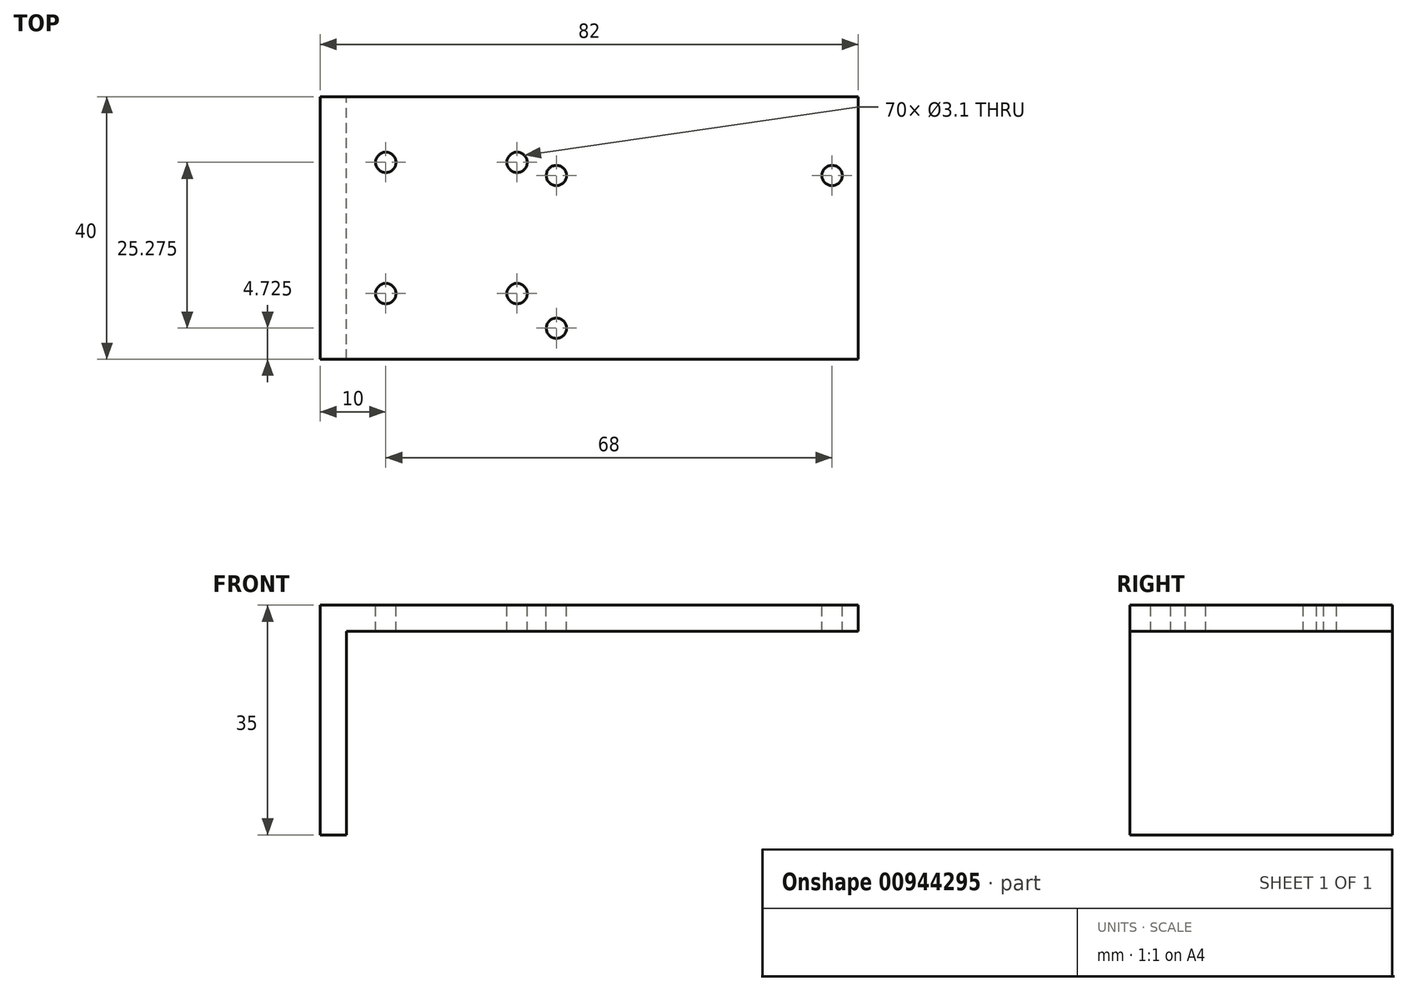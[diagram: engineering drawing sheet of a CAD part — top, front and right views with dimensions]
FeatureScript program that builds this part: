
annotation { "Feature Type Name" : "Feature", "Feature Type Description" : "" }
export const myFeature = defineFeature(function(context is Context, id is Id, definition is map)
    precondition{}
    {
        {
            var Q0;
            Q0=qCreatedBy(makeId("Front.planeOp"),FACE);
            var sketch = newSketch(context, id + "F0", { "sketchPlane" : qUnion([Q0])});
            skLineSegment(sketch, "E0", {"start": v(0, 0) * mm, "end": v(0, -35) * mm});
            skLineSegment(sketch, "E1", {"start": v(0, -35) * mm, "end": v(4, -35) * mm});
            skLineSegment(sketch, "E2", {"start": v(4, -35) * mm, "end": v(4, -4) * mm});
            skLineSegment(sketch, "E3", {"start": v(4, -4) * mm, "end": v(82, -4) * mm});
            skLineSegment(sketch, "E4", {"start": v(82, -4) * mm, "end": v(82, 0) * mm});
            skLineSegment(sketch, "E5", {"start": v(82, 0) * mm, "end": v(0, 0) * mm});
            skSolve(sketch);
        }
        {
            var Q0;
            Q0=makeQuery(id+"F0.imprint","IMPRINT",FACE,{"disambiguationData":[TD([[makeQuery(id+"F0.imprint","IMPRINT",EDGE,{"derivedFrom":sQuery(id+"F0.wireOp",EDGE,"E0")}),1.0]])]});
            extrude(context, id + "F1", {"entities" : qUnion([Q0]), "depth" : 40 * mm, "offsetDistance" : 25 * mm});
        }
        {
            var Q0;
            Q0=makeQuery(id+"F1.opExtrude","SWEPT_FACE",FACE,{"disambiguationData":[OSD([sQuery(id+"F0.wireOp",EDGE,"E5")])]});
            var sketch = newSketch(context, id + "F2", { "sketchPlane" : qUnion([Q0])});
            skLineSegment(sketch, "E6", {"start": v(0, -20) * mm, "end": v(82, -20) * mm, "construction": true});
            skLineSegment(sketch, "E7", {"start": v(20, 0) * mm, "end": v(20, -40) * mm, "construction": true});
            skCircle(sketch, "E8", {"center": v(30, -10) * mm, "radius": 1.55 * mm});
            skCircle(sketch, "E9.MirrorC", {"center": v(10, -10) * mm, "radius": 1.55 * mm});
            skCircle(sketch, "E10.MirrorC", {"center": v(10, -30) * mm, "radius": 1.55 * mm});
            skCircle(sketch, "E11.MirrorC", {"center": v(30, -30) * mm, "radius": 1.55 * mm});
            skLineSegment(sketch, "E12", {"start": v(36, -40) * mm, "end": v(36, 0) * mm, "construction": true});
            skCircle(sketch, "E13", {"center": v(36, -35.27) * mm, "radius": 1.55 * mm});
            skCircle(sketch, "E14", {"center": v(36, -12) * mm, "radius": 1.55 * mm});
            skCircle(sketch, "E15", {"center": v(78, -12) * mm, "radius": 1.55 * mm});
            skLineSegment(sketch, "E16", {"start": v(36, -12) * mm, "end": v(63.08, -12) * mm, "construction": true});
            skSolve(sketch);
        }
        {
            var Q0;
            Q0=qSketchRegion(id+"F2",true);
            extrude(context, id + "F3", {"entities" : qUnion([Q0]), "operationType" : NewBodyOperationType.REMOVE, "endBound" : BoundingType.UP_TO_NEXT, "oppositeDirection" : true, "depth" : 25 * mm, "offsetDistance" : 25 * mm});
        }
    });
